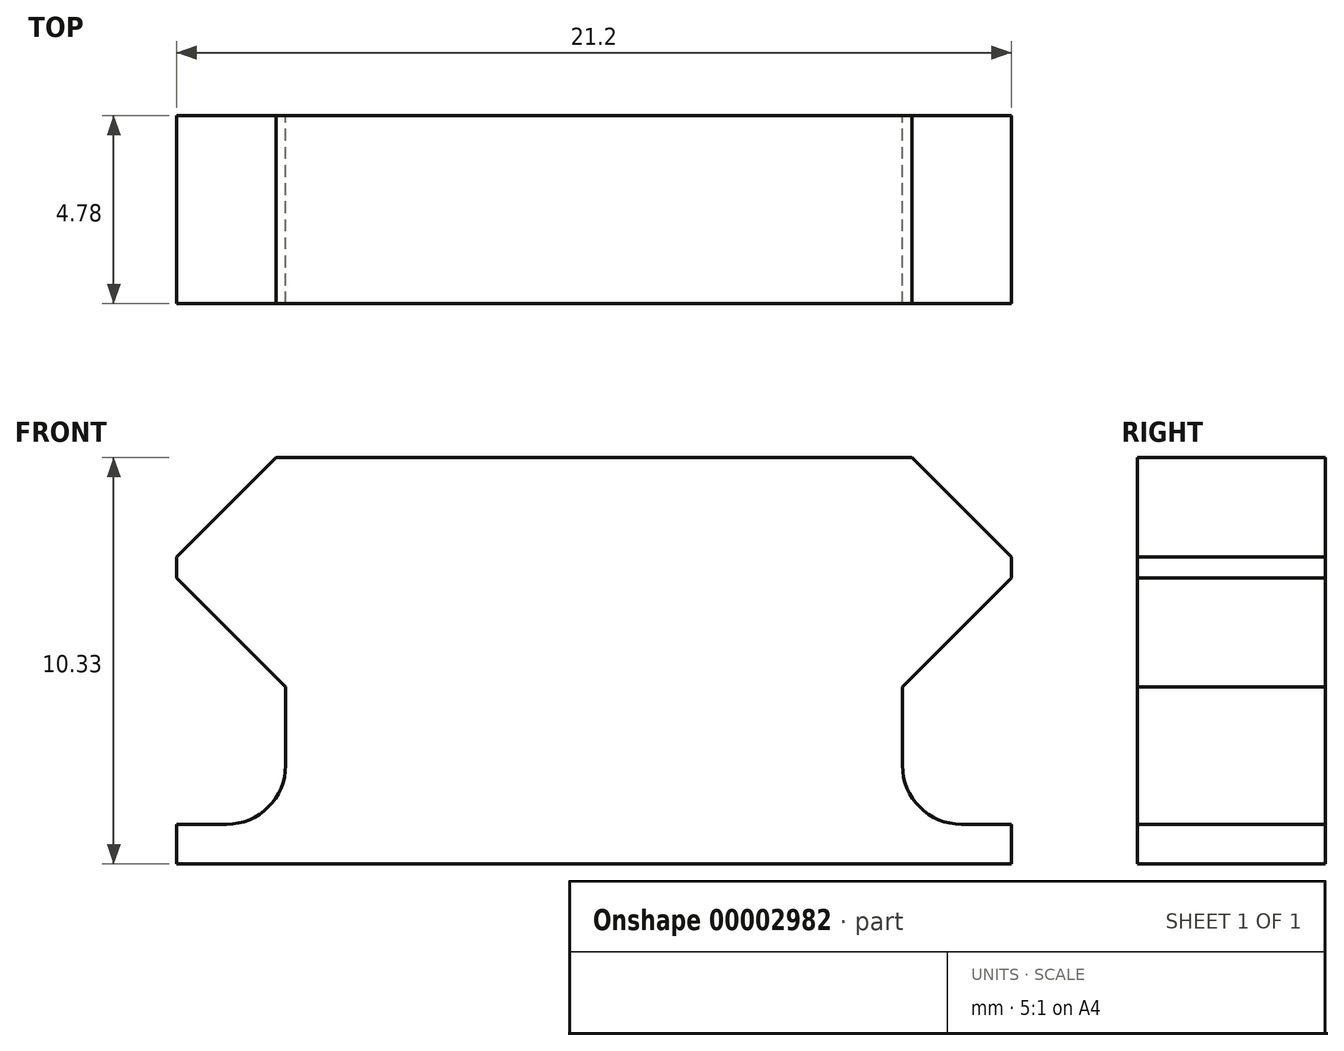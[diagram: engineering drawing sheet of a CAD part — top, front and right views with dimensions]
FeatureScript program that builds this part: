
annotation { "Feature Type Name" : "Feature", "Feature Type Description" : "" }
export const myFeature = defineFeature(function(context is Context, id is Id, definition is map)
    precondition{}
    {
        {
            var Q0;
            Q0=qCreatedBy(makeId("Front.planeOp"),FACE);
            var sketch = newSketch(context, id + "F0", { "sketchPlane" : qUnion([Q0])});
            skLineSegment(sketch, "E0", {"start": v(0, 15.8) * mm, "end": v(0, -17.85) * mm, "construction": true});
            skLineSegment(sketch, "E1", {"start": v(-10.6, -4.36) * mm, "end": v(0, -4.36) * mm});
            skLineSegment(sketch, "E2.0.MirrorCS", {"start": v(10.6, -4.36) * mm, "end": v(0, -4.36) * mm});
            skLineSegment(sketch, "E3", {"start": v(-10.6, -4.36) * mm, "end": v(-10.6, -3.36) * mm});
            skLineSegment(sketch, "E4", {"start": v(-10.6, -3.36) * mm, "end": v(-9.34, -3.36) * mm});
            skLineSegment(sketch, "E5", {"start": v(10.6, -4.36) * mm, "end": v(10.6, -3.36) * mm});
            skLineSegment(sketch, "E6", {"start": v(10.6, -3.36) * mm, "end": v(9.34, -3.36) * mm});
            skLineSegment(sketch, "E7", {"start": v(-7.84, -1.86) * mm, "end": v(-7.84, 5.97) * mm});
            skLineSegment(sketch, "E8.0.MirrorCS", {"start": v(7.84, -1.86) * mm, "end": v(7.84, 5.97) * mm});
            skLineSegment(sketch, "E9", {"start": v(-10.6, -8.18) * mm, "end": v(-10.6, 7.36) * mm, "construction": true});
            skPoint(sketch, "E10.newPointA", {"position": v(7.84, -3.36) * mm});
            skArc(sketch, "E10.filletArc", {"start": v(7.84, -1.86) * mm, "mid": v(8.27, -2.92) * mm, "end": v(9.34, -3.36) * mm});
            skPoint(sketch, "E11.newPointA", {"position": v(-7.84, -3.36) * mm});
            skPoint(sketch, "E11.newPointB", {"position": v(0, -3.36) * mm});
            skArc(sketch, "E11.filletArc", {"start": v(-9.34, -3.36) * mm, "mid": v(-8.27, -2.92) * mm, "end": v(-7.84, -1.86) * mm});
            skLineSegment(sketch, "E12", {"start": v(-11.77, 5.97) * mm, "end": v(12.47, 5.97) * mm, "construction": true});
            skLineSegment(sketch, "E13", {"start": v(9.5, 5.97) * mm, "end": v(9.5, 1.8) * mm, "construction": true});
            skLineSegment(sketch, "E14", {"start": v(9.5, 1.8) * mm, "end": v(-12.15, 1.8) * mm, "construction": true});
            skLineSegment(sketch, "E15", {"start": v(-12.35, 4.54) * mm, "end": v(10.6, 4.54) * mm, "construction": true});
            skLineSegment(sketch, "E16", {"start": v(10.6, -4.36) * mm, "end": v(10.6, 9.86) * mm, "construction": true});
            skLineSegment(sketch, "E17.0.MirrorCS", {"start": v(-9.5, 5.97) * mm, "end": v(-9.5, 1.8) * mm, "construction": true});
            skLineSegment(sketch, "E18", {"start": v(9.5, 4.54) * mm, "end": v(10.6, 3.44) * mm});
            skLineSegment(sketch, "E19", {"start": v(9.5, 1.8) * mm, "end": v(10.6, 2.9) * mm});
            skLineSegment(sketch, "E20", {"start": v(10.6, 3.44) * mm, "end": v(10.6, 2.9) * mm});
            skLineSegment(sketch, "E21", {"start": v(9.5, 4.54) * mm, "end": v(8.08, 5.97) * mm});
            skLineSegment(sketch, "E22", {"start": v(8.08, 5.97) * mm, "end": v(-7.84, 5.97) * mm});
            skLineSegment(sketch, "E23", {"start": v(10.6, 2.9) * mm, "end": v(7.84, 0.14) * mm});
            skLineSegment(sketch, "E24.0.MirrorCS", {"start": v(-10.6, 2.9) * mm, "end": v(-7.84, 0.14) * mm});
            skLineSegment(sketch, "E25.0.MirrorCS", {"start": v(-9.5, 4.54) * mm, "end": v(-10.6, 3.44) * mm});
            skLineSegment(sketch, "E26.0.MirrorCS", {"start": v(-9.5, 4.54) * mm, "end": v(-8.08, 5.97) * mm});
            skLineSegment(sketch, "E27.0.MirrorCS", {"start": v(-10.6, 3.44) * mm, "end": v(-10.6, 2.9) * mm});
            skLineSegment(sketch, "E28", {"start": v(-8.08, 5.97) * mm, "end": v(-7.84, 5.97) * mm});
            skLineSegment(sketch, "E29", {"start": v(7.84, 0.14) * mm, "end": v(-7.84, 0.14) * mm});
            skSolve(sketch);
        }
        {
            var Q0;
            Q0 = qSketchRegion(id + "F0", true);
            extrude(context, id + "F1", {"entities" : qUnion([Q0]), "depth" : 4.78 * mm});
        }
    });
